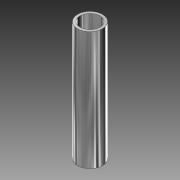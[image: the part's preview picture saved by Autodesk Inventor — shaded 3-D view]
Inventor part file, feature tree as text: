
AUTODESK INVENTOR PART (.ipt)
format: ipt  version: 2012 (Build 160160000, 160)  size: 74,240 bytes
history: native  units: mm
features: extrude x1, sketch x1
ambient origin geometry x8: Origin, YZ Plane, XZ Plane, XY Plane, X Axis, Y Axis, Z Axis, Center Point
bodies: Solid1 (feature_tree)
feature tree (2):
  extrude  "Extrusion1"  Depth=5.715mm
  sketch  "Sketch1"  dims[d0=7.14375mm d1=5.715mm d2=34.0mm d3=0.0mm]
